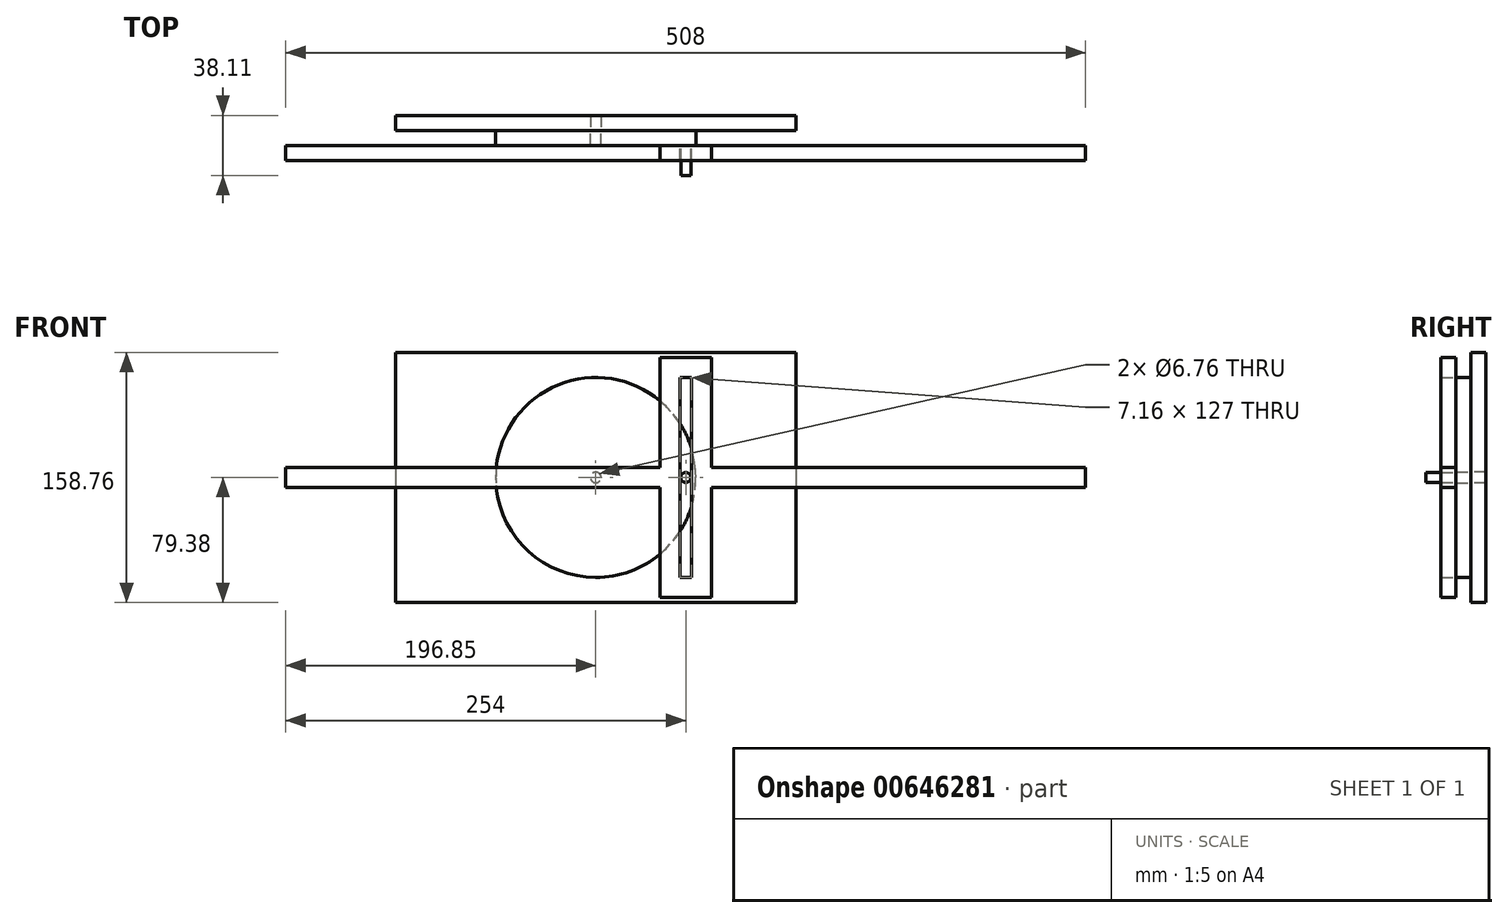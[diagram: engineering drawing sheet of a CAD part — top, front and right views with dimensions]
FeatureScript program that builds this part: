
annotation { "Feature Type Name" : "Feature", "Feature Type Description" : "" }
export const myFeature = defineFeature(function(context is Context, id is Id, definition is map)
    precondition{}
    {
        {
            assignVariable(context, id + "F0", {"name" : "mat", "anyValue" : 9.52 * mm});
        }
        {
            var Q0;
            Q0=qCreatedBy(makeId("Front.planeOp"),FACE);
            var sketch = newSketch(context, id + "F1", { "sketchPlane" : qUnion([Q0])});
            skCircle(sketch, "E0", {"center": v(0, 0) * mm, "radius": 3.38 * mm});
            skCircle(sketch, "E1", {"center": v(0, 0) * mm, "radius": 63.5 * mm});
            skSolve(sketch);
        }
        {
            var Q0;
            Q0=makeQuery(id+"F1.imprint","IMPRINT",FACE,{"disambiguationData":[TD([[makeQuery(id+"F1.imprint","IMPRINT",EDGE,{"derivedFrom":sQuery(id+"F1.wireOp",EDGE,"E0")}),-1.0]])]});
            extrude(context, id + "F2", {"entities" : qUnion([Q0]), "depth" : getVariable(context, 'mat'), "offsetDistance" : 25.4 * mm});
        }
        {
            var Q0;
            Q0=makeQuery(id+"F2.opExtrude","CAP_FACE",FACE,{"disambiguationData":[OSD([sQuery(id+"F1.wireOp",EDGE,"E0"),sQuery(id+"F1.wireOp",EDGE,"E1")])],"isStart":false});
            var sketch = newSketch(context, id + "F3", { "sketchPlane" : qUnion([Q0])});
            skCircle(sketch, "E2", {"center": v(57.15, 0) * mm, "radius": 3.18 * mm});
            skLineSegment(sketch, "E3.bottom", {"start": v(53.57, 63.5) * mm, "end": v(60.73, 63.5) * mm});
            skLineSegment(sketch, "E3.top", {"start": v(53.57, -63.5) * mm, "end": v(60.73, -63.5) * mm});
            skLineSegment(sketch, "E3.left", {"start": v(53.57, 63.5) * mm, "end": v(53.57, -63.5) * mm});
            skLineSegment(sketch, "E3.right", {"start": v(60.73, 63.5) * mm, "end": v(60.73, -63.5) * mm});
            skLineSegment(sketch, "E4", {"start": v(57.15, 63.5) * mm, "end": v(57.15, -63.5) * mm, "construction": true});
            skLineSegment(sketch, "E5.bottom", {"start": v(-196.85, 6.35) * mm, "end": v(311.15, 6.35) * mm});
            skLineSegment(sketch, "E5.top", {"start": v(-196.85, -6.35) * mm, "end": v(311.15, -6.35) * mm});
            skLineSegment(sketch, "E5.left", {"start": v(-196.85, 6.35) * mm, "end": v(-196.85, -6.35) * mm});
            skLineSegment(sketch, "E5.right", {"start": v(311.15, 6.35) * mm, "end": v(311.15, -6.35) * mm});
            skLineSegment(sketch, "E6.bottom", {"start": v(73.42, -76.2) * mm, "end": v(40.88, -76.2) * mm});
            skLineSegment(sketch, "E6.top", {"start": v(73.42, 76.2) * mm, "end": v(40.88, 76.2) * mm});
            skLineSegment(sketch, "E6.left", {"start": v(73.42, -76.2) * mm, "end": v(73.42, 76.2) * mm});
            skLineSegment(sketch, "E6.right", {"start": v(40.88, -76.2) * mm, "end": v(40.88, 76.2) * mm});
            skSolve(sketch);
        }
        {
            var Q0;
            Q0=makeQuery(id+"F3.imprint","IMPRINT",FACE,{"disambiguationData":[TD([[makeQuery(id+"F3.imprint","IMPRINT",EDGE,{"derivedFrom":sQuery(id+"F3.wireOp",EDGE,"E2")}),1.0]])]});
            extrude(context, id + "F4", {"entities" : qUnion([Q0]), "operationType" : NewBodyOperationType.ADD, "depth" : getVariable(context, 'mat') * 2, "offsetDistance" : 25.4 * mm});
        }
        {
            var Q0;
            Q0=qSketchRegion(id+"F3",true);
            extrude(context, id + "F5", {"entities" : qUnion([Q0]), "depth" : getVariable(context, 'mat'), "offsetDistance" : 25.4 * mm});
        }
        {
            var Q0;
            Q0=makeQuery(id+"F2.opExtrude","CAP_FACE",FACE,{"disambiguationData":[OSD([sQuery(id+"F1.wireOp",EDGE,"E0"),sQuery(id+"F1.wireOp",EDGE,"E1")])],"isStart":true});
            var sketch = newSketch(context, id + "F6", { "sketchPlane" : qUnion([Q0])});
            skLineSegment(sketch, "E7.bottom", {"start": v(-127, 79.38) * mm, "end": v(127, 79.38) * mm});
            skLineSegment(sketch, "E7.top", {"start": v(-127, -79.38) * mm, "end": v(127, -79.38) * mm});
            skLineSegment(sketch, "E7.left", {"start": v(-127, 79.38) * mm, "end": v(-127, -79.38) * mm});
            skLineSegment(sketch, "E7.right", {"start": v(127, 79.38) * mm, "end": v(127, -79.38) * mm});
            skPoint(sketch, "E7.middle", {"position": v(0, 0) * mm});
            skSolve(sketch);
        }
        {
            var Q0;
            Q0=makeQuery(id+"F6.imprint","IMPRINT",FACE,{"disambiguationData":[TD([[makeQuery(id+"F6.imprint","IMPRINT",EDGE,{"derivedFrom":sQuery(id+"F6.wireOp",EDGE,"E7.bottom")}),-1.0]])]});
            var Q1;
            Q1=makeQuery(id+"F6.imprint","IMPRINT",FACE,{"disambiguationData":[TD([[makeQuery(id+"F6.imprint","IMPRINT",EDGE,{"derivedFrom":makeQuery(id+"F2.opExtrude","CAP_EDGE",EDGE,{"disambiguationData":[OSD([sQuery(id+"F1.wireOp",EDGE,"E0")])],"isStart":true})}),1.0]])]});
            extrude(context, id + "F7", {"entities" : qUnion([Q0, Q1]), "depth" : getVariable(context, 'mat'), "offsetDistance" : 25.4 * mm});
        }
    });
